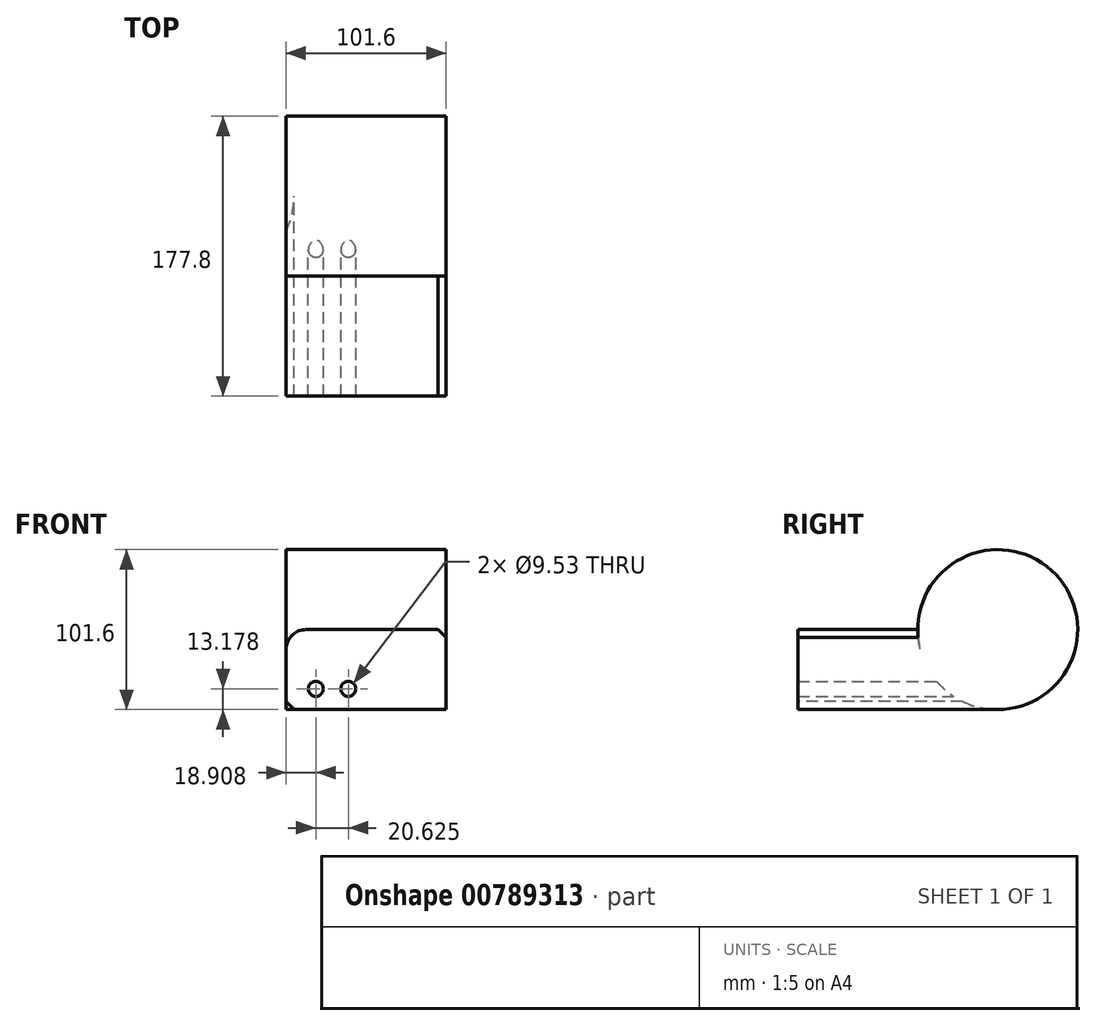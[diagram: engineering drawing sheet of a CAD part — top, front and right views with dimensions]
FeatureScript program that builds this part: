
annotation { "Feature Type Name" : "Feature", "Feature Type Description" : "" }
export const myFeature = defineFeature(function(context is Context, id is Id, definition is map)
    precondition{}
    {
        {
            var Q0;
            Q0=qCreatedBy(makeId("Front.planeOp"),FACE);
            var sketch = newSketch(context, id + "F0", { "sketchPlane" : qUnion([Q0])});
            skLineSegment(sketch, "E0.bottom", {"start": v(50.8, -25.4) * mm, "end": v(-50.8, -25.4) * mm});
            skLineSegment(sketch, "E0.top", {"start": v(50.8, 25.4) * mm, "end": v(-50.8, 25.4) * mm});
            skLineSegment(sketch, "E0.left", {"start": v(50.8, -25.4) * mm, "end": v(50.8, 25.4) * mm});
            skLineSegment(sketch, "E0.right", {"start": v(-50.8, -25.4) * mm, "end": v(-50.8, 25.4) * mm});
            skPoint(sketch, "E0.middle", {"position": v(0, 0) * mm});
            skSolve(sketch);
        }
        {
            var Q0;
            Q0=makeQuery(id+"F0.imprint","IMPRINT",FACE,{"disambiguationData":[TD([[makeQuery(id+"F0.imprint","IMPRINT",EDGE,{"derivedFrom":sQuery(id+"F0.wireOp",EDGE,"E0.bottom")}),-1.0]])]});
            extrude(context, id + "F1", {"entities" : qUnion([Q0]), "depth" : 127 * mm, "offsetDistance" : 25.4 * mm});
        }
        {
            var Q0;
            Q0=makeQuery(id+"F1.opExtrude","CAP_FACE",FACE,{"disambiguationData":[OSD([sQuery(id+"F0.wireOp",EDGE,"E0.bottom"),sQuery(id+"F0.wireOp",EDGE,"E0.top"),sQuery(id+"F0.wireOp",EDGE,"E0.left"),sQuery(id+"F0.wireOp",EDGE,"E0.right")])],"isStart":true});
            var sketch = newSketch(context, id + "F2", { "sketchPlane" : qUnion([Q0])});
            skCircle(sketch, "E1", {"center": v(31.9, -12.22) * mm, "radius": 4.76 * mm});
            skCircle(sketch, "E2", {"center": v(11.27, -12.22) * mm, "radius": 4.76 * mm});
            skSolve(sketch);
        }
        {
            var Q0;
            Q0 = qSketchRegion(id + "F2", true);
            extrude(context, id + "F3", {"entities" : qUnion([Q0]), "operationType" : NewBodyOperationType.REMOVE, "oppositeDirection" : true, "depth" : 158.24 * mm, "offsetDistance" : 25.4 * mm});
        }
        {
            var Q0;
            Q0=makeQuery(id+"F1.opExtrude","SWEPT_EDGE",EDGE,{"disambiguationData":[OSD([sQuery(id+"F0.wireOp",EDGE,"E0.top"),sQuery(id+"F0.wireOp",EDGE,"E0.right")])]});
            fillet(context, id + "F4", {"entities" : qUnion([Q0]), "radius" : 12.7 * mm, "tangentPropagation" : true, "allowEdgeOverflow" : false});
        }
        {
            var Q0;
            Q0=makeQuery(id+"F1.opExtrude","SWEPT_EDGE",EDGE,{"disambiguationData":[OSD([sQuery(id+"F0.wireOp",EDGE,"E0.top"),sQuery(id+"F0.wireOp",EDGE,"E0.left")])]});
            var Q1;
            Q1=makeQuery(id+"F1.opExtrude","SWEPT_EDGE",EDGE,{"disambiguationData":[OSD([sQuery(id+"F0.wireOp",EDGE,"E0.bottom"),sQuery(id+"F0.wireOp",EDGE,"E0.right")])]});
            chamfer(context, id + "F5", {"entities" : qUnion([Q0, Q1]), "width" : 5.08 * mm, "tangentPropagation" : true});
        }
        {
            var Q0;
            Q0=makeQuery(id+"F0.imprint","IMPRINT",FACE,{"disambiguationData":[TD([[makeQuery(id+"F0.imprint","IMPRINT",EDGE,{"derivedFrom":sQuery(id+"F0.wireOp",EDGE,"E0.bottom")}),-1.0]])]});
            var Q1;
            Q1=sQuery(id+"F0.wireOp",EDGE,"E0.top");
            revolve(context, id + "F6", {"operationType" : NewBodyOperationType.ADD, "surfaceOperationType" : NewSurfaceOperationType.NEW, "entities" : qUnion([Q0]), "axis" : qUnion([Q1]), "revolveType" : RevolveType.FULL});
        }
    });
